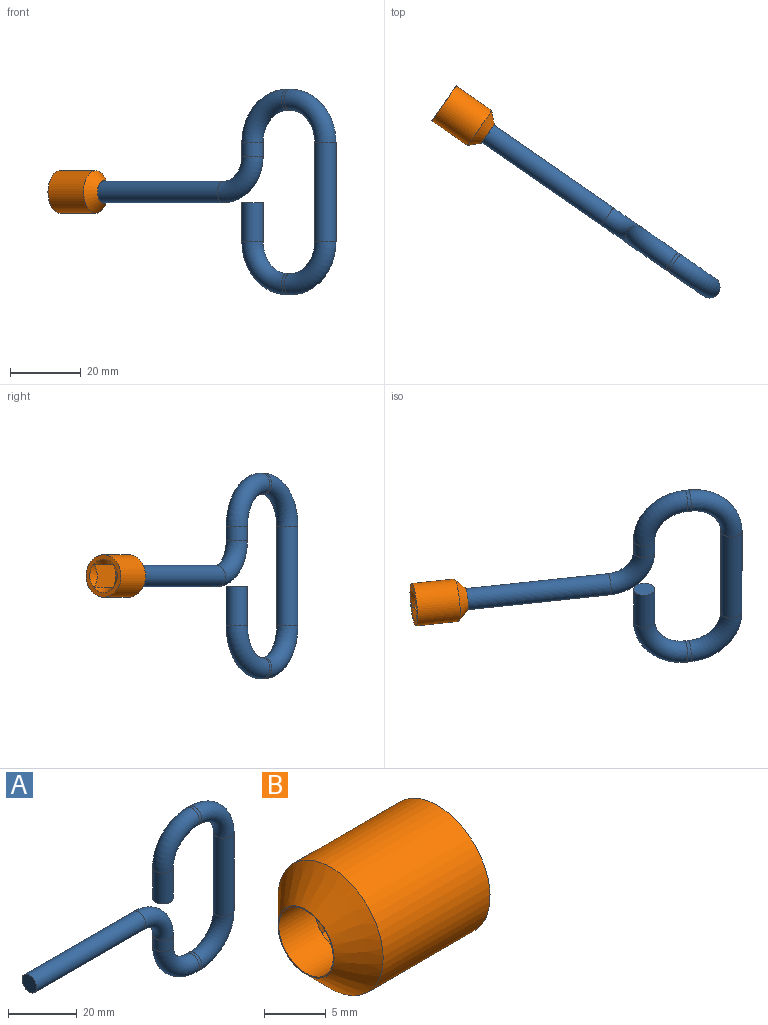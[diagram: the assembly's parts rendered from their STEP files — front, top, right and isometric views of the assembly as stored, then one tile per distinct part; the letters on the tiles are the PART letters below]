
ASSEMBLY  parts=2 mates=1
PART A: 13 faces, bbox 84.2x6x60.5 mm
  f0: plane 6x6mm, normal (-1,0,0), area 28.3mm2, adj f2
  f1: plane 6x6mm, normal (0,0,-1), area 28.3mm2, adj f12
  f2: cylinder r=3mm len=45mm, axis (1,0,0), area 848.2mm2, adj f0,f3
  f3: torus R=10mm, axis (0,1,0), area 296.1mm2, adj f2,f4
  f4: cylinder r=3mm len=6mm, axis (0,0,-1), area 75.4mm2, adj f3,f5
  f5: torus R=12mm, axis (0,-1,0), area 355.3mm2, adj f4,f6
  f6: cylinder r=3mm len=6mm, axis (1,0,0), area 18.8mm2, adj f5,f7
  f7: torus R=12mm, axis (0,-1,0), area 355.3mm2, adj f6,f8
  f8: cylinder r=3mm len=28mm, axis (0,0,1), area 527.8mm2, adj f7,f9
  f9: torus R=12mm, axis (0,-1,0), area 355.3mm2, adj f8,f10
  f10: cylinder r=3mm len=6mm, axis (-1,0,0), area 18.8mm2, adj f9,f11
  f11: torus R=12mm, axis (0,-1,0), area 355.3mm2, adj f10,f12
  f12: cylinder r=3mm len=11mm, axis (0,0,-1), area 207.3mm2, adj f1,f11
PART B: 11 faces, bbox 15x12x12 mm
  f0: cone r=3.2mm half-angle=45deg, axis (1,0,0), area 40.2mm2, adj f3,f7,f8,f9,f10
  f1: cylinder r=3.1mm len=6.2mm, axis (-1,0,0), area 77.9mm2, adj f4,f5
  f2: cylinder r=6mm len=12.2mm, axis (-1,0,0), area 459.9mm2, adj f3,f6
  f3: plane 12x12mm, normal (1,0,0), area 43.7mm2, adj f0,f2
  f4: plane 6.4x6.4mm, normal (-1,0,0), area 2mm2, adj f1,f6
  f5: plane 6.4x6.4mm, normal (1,0,0), area 10.8mm2, adj f1,f7,f8,f9,f10
  f6: cone r=6mm half-angle=45deg, axis (1,0,0), area 114.4mm2, adj f2,f4
  f7: plane 10.83x6.41mm, normal (0,-1,0), area 63.8mm2, adj f0,f5,f8,f10
  f8: plane 10.83x6.41mm, normal (0,0,-1), area 63.8mm2, adj f0,f5,f7,f9
  f9: plane 10.83x6.41mm, normal (0,1,0), area 63.8mm2, adj f0,f5,f8,f10
  f10: plane 10.83x6.41mm, normal (0,0,1), area 63.8mm2, adj f0,f5,f7,f9
PLACE A rot(axis=(-0.95,0.3,0),180deg) t=(11.77,-4.32,2.11)mm
PLACE B rot(axis=(0,0,1),145.3deg) t=(15.06,-6.6,2.11)mm
MATE slider A.f2 <-> B.f1  axis (-0.82,0.57,0) through (11.77,-4.32,2.11)mm
